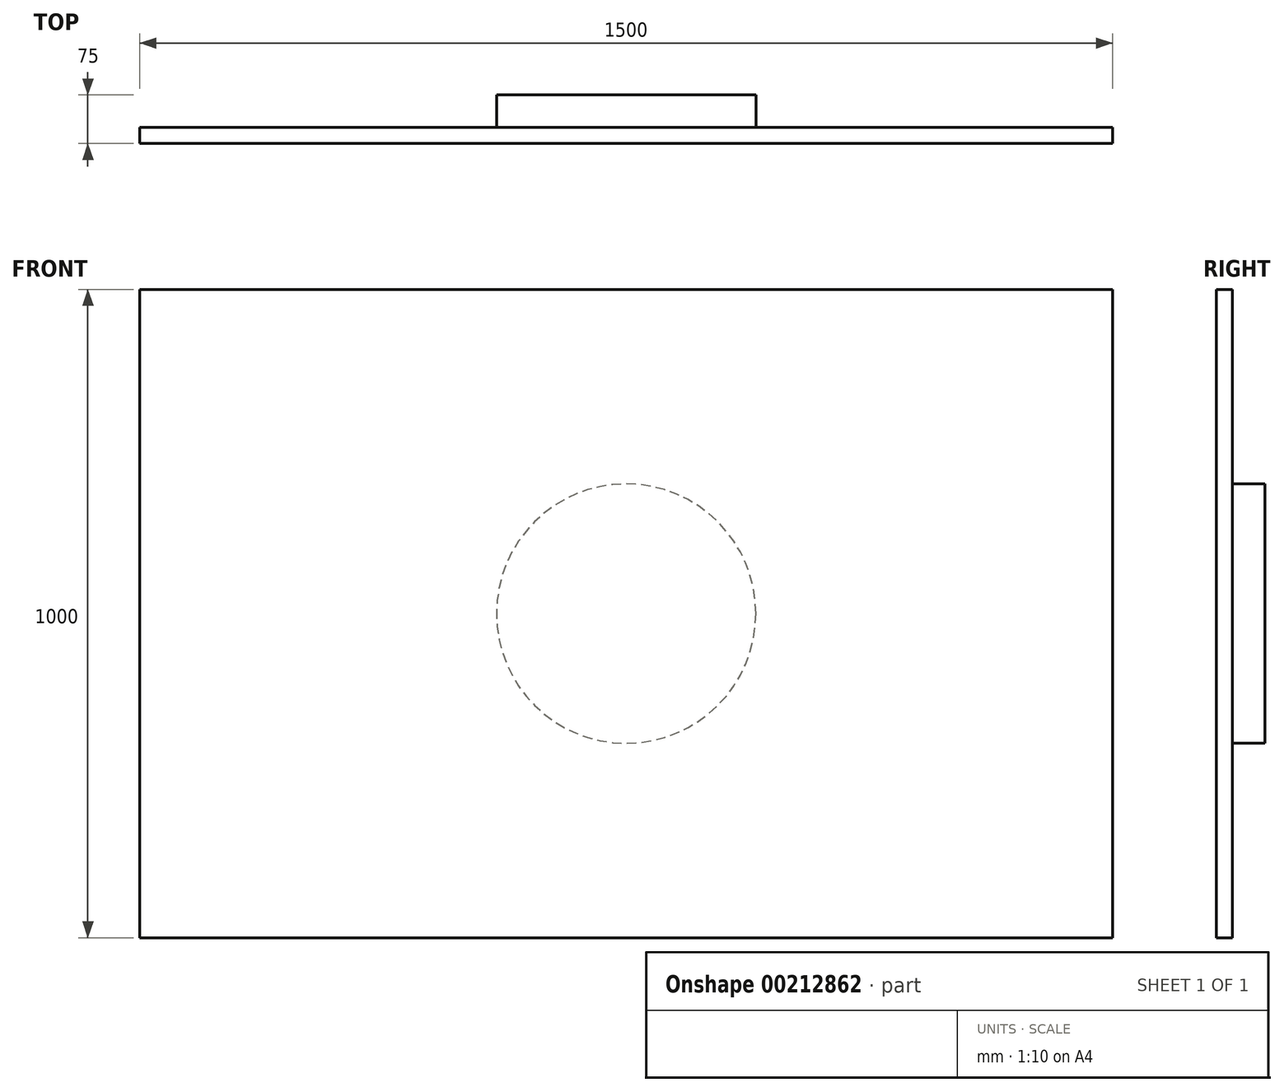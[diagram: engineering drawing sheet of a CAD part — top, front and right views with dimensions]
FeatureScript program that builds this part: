
annotation { "Feature Type Name" : "Feature", "Feature Type Description" : "" }
export const myFeature = defineFeature(function(context is Context, id is Id, definition is map)
    precondition{}
    {
        {
            var Q0;
            Q0=qCreatedBy(makeId("Front.planeOp"),FACE);
            var sketch = newSketch(context, id + "F0", { "sketchPlane" : qUnion([Q0])});
            skLineSegment(sketch, "E0.bottom", {"start": v(0, 0) * mm, "end": v(1500, 0) * mm});
            skLineSegment(sketch, "E0.top", {"start": v(0, 1000) * mm, "end": v(1500, 1000) * mm});
            skLineSegment(sketch, "E0.left", {"start": v(0, 0) * mm, "end": v(0, 1000) * mm});
            skLineSegment(sketch, "E0.right", {"start": v(1500, 0) * mm, "end": v(1500, 1000) * mm});
            skSolve(sketch);
        }
        {
            var Q0;
            Q0 = qSketchRegion(id + "F0", true);
            extrude(context, id + "F1", {"entities" : qUnion([Q0]), "depth" : 25 * mm});
        }
        {
            var Q0;
            Q0=makeQuery(id+"F1.opExtrude","CAP_FACE",FACE,{"disambiguationData":[OSD([sQuery(id+"F0.wireOp",EDGE,"E0.bottom"),sQuery(id+"F0.wireOp",EDGE,"E0.top"),sQuery(id+"F0.wireOp",EDGE,"E0.left"),sQuery(id+"F0.wireOp",EDGE,"E0.right")])],"isStart":true});
            var sketch = newSketch(context, id + "F2", { "sketchPlane" : qUnion([Q0])});
            skCircle(sketch, "E1", {"center": v(-750, 500) * mm, "radius": 200 * mm});
            skPoint(sketch, "E1.centerSnap0", {"position": v(-1500, 500) * mm});
            skPoint(sketch, "E1.centerSnap1", {"position": v(-750, 1000) * mm});
            skSolve(sketch);
        }
        {
            var Q0;
            Q0 = qSketchRegion(id + "F2", true);
            extrude(context, id + "F3", {"entities" : qUnion([Q0]), "operationType" : NewBodyOperationType.ADD, "depth" : 50 * mm});
        }
    });
